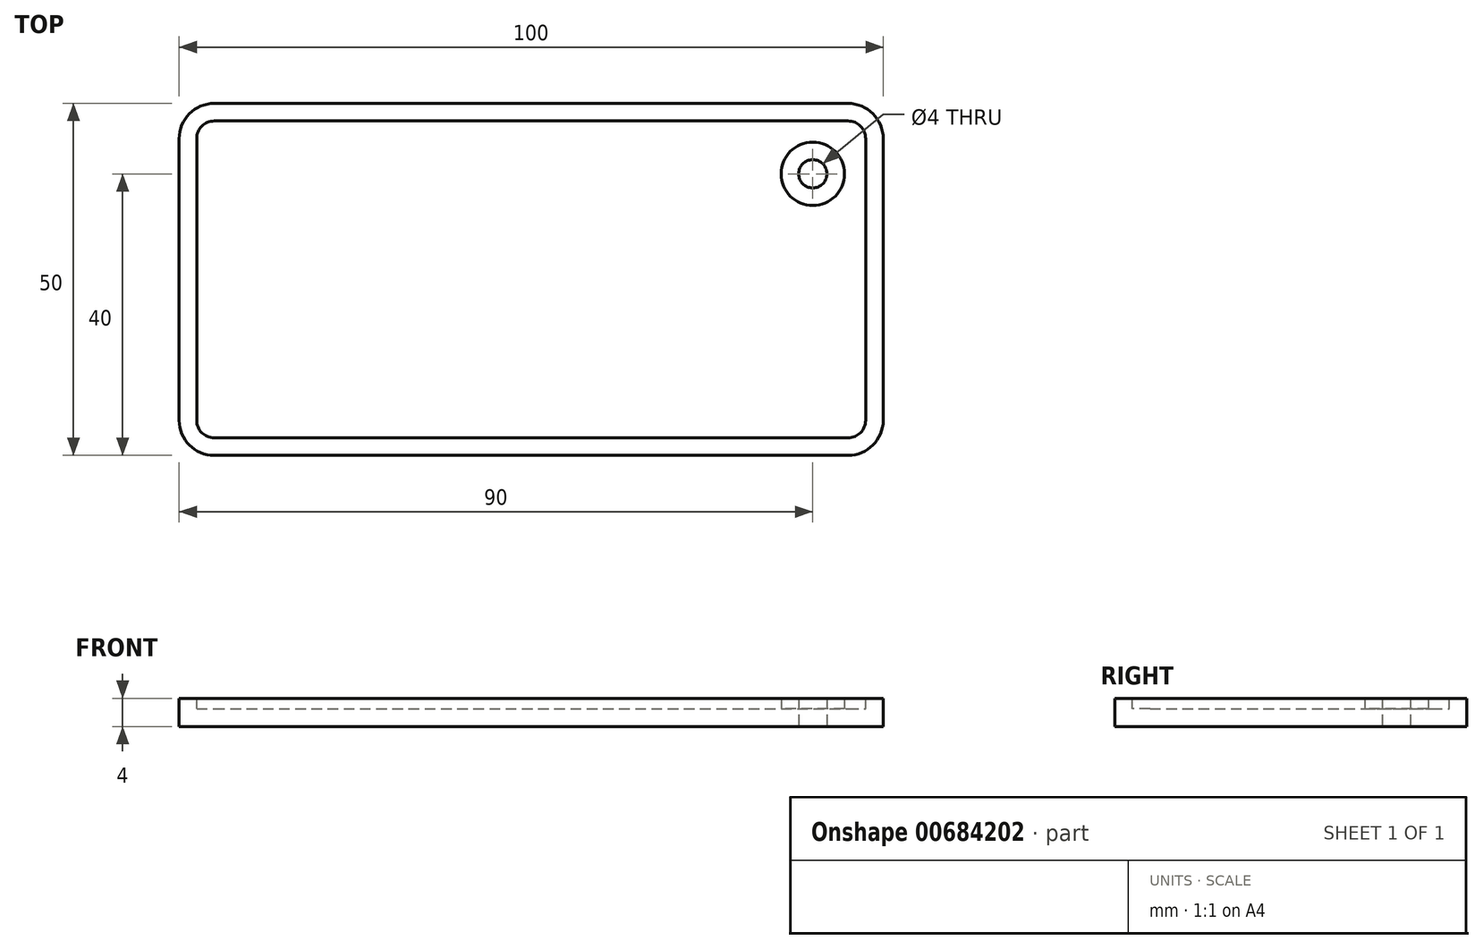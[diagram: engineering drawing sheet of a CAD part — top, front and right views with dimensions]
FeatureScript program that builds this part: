
annotation { "Feature Type Name" : "Feature", "Feature Type Description" : "" }
export const myFeature = defineFeature(function(context is Context, id is Id, definition is map)
    precondition{}
    {
        {
            var Q0;
            Q0=qCreatedBy(makeId("Top.planeOp"),FACE);
            var sketch = newSketch(context, id + "F0", { "sketchPlane" : qUnion([Q0])});
            skLineSegment(sketch, "E0.bottom", {"start": v(5, 0) * mm, "end": v(95, 0) * mm});
            skLineSegment(sketch, "E0.top", {"start": v(5, 50) * mm, "end": v(95, 50) * mm});
            skLineSegment(sketch, "E0.left", {"start": v(0, 5) * mm, "end": v(0, 45) * mm});
            skLineSegment(sketch, "E0.right", {"start": v(100, 5) * mm, "end": v(100, 45) * mm});
            skLineSegment(sketch, "E1.bottom", {"start": v(10, 45) * mm, "end": v(90, 45) * mm});
            skLineSegment(sketch, "E1.top", {"start": v(10, 5) * mm, "end": v(90, 5) * mm});
            skLineSegment(sketch, "E1.left", {"start": v(5, 40) * mm, "end": v(5, 10) * mm});
            skLineSegment(sketch, "E1.right", {"start": v(95, 40) * mm, "end": v(95, 10) * mm});
            skPoint(sketch, "E2.visualSharp", {"position": v(5, 45) * mm});
            skArc(sketch, "E2.filletArc", {"start": v(10, 45) * mm, "mid": v(6.46, 43.54) * mm, "end": v(5, 40) * mm});
            skPoint(sketch, "E3.visualSharp", {"position": v(95, 45) * mm});
            skArc(sketch, "E3.filletArc", {"start": v(95, 40) * mm, "mid": v(93.54, 43.54) * mm, "end": v(90, 45) * mm});
            skPoint(sketch, "E4.visualSharp", {"position": v(95, 5) * mm});
            skArc(sketch, "E4.filletArc", {"start": v(90, 5) * mm, "mid": v(93.54, 6.46) * mm, "end": v(95, 10) * mm});
            skPoint(sketch, "E5.visualSharp", {"position": v(5, 5) * mm});
            skArc(sketch, "E5.filletArc", {"start": v(5, 10) * mm, "mid": v(6.46, 6.46) * mm, "end": v(10, 5) * mm});
            skPoint(sketch, "E6.visualSharp", {"position": v(0, 0) * mm});
            skArc(sketch, "E6.filletArc", {"start": v(0, 5) * mm, "mid": v(1.46, 1.46) * mm, "end": v(5, 0) * mm});
            skPoint(sketch, "E7.visualSharp", {"position": v(100, 0) * mm});
            skArc(sketch, "E7.filletArc", {"start": v(95, 0) * mm, "mid": v(98.54, 1.46) * mm, "end": v(100, 5) * mm});
            skPoint(sketch, "E8.visualSharp", {"position": v(0, 50) * mm});
            skArc(sketch, "E8.filletArc", {"start": v(5, 50) * mm, "mid": v(1.46, 48.54) * mm, "end": v(0, 45) * mm});
            skPoint(sketch, "E9.visualSharp", {"position": v(100, 50) * mm});
            skArc(sketch, "E9.filletArc", {"start": v(100, 45) * mm, "mid": v(98.54, 48.54) * mm, "end": v(95, 50) * mm});
            skSolve(sketch);
        }
        {
            var Q0;
            Q0=makeQuery(id+"F0.imprint","IMPRINT",FACE,{"disambiguationData":[TD([[makeQuery(id+"F0.imprint","IMPRINT",EDGE,{"derivedFrom":sQuery(id+"F0.wireOp",EDGE,"E1.bottom")}),-1.0]])]});
            var Q1;
            Q1=makeQuery(id+"F0.imprint","IMPRINT",FACE,{"disambiguationData":[TD([[makeQuery(id+"F0.imprint","IMPRINT",EDGE,{"derivedFrom":sQuery(id+"F0.wireOp",EDGE,"E0.bottom")}),1.0]])]});
            extrude(context, id + "F1", {"entities" : qUnion([Q0, Q1]), "depth" : 4 * mm, "offsetDistance" : 25 * mm});
        }
        {
            var Q0;
            Q0=sQuery(id+"F0.wireOp",VERTEX,"E3.filletArc.center");
            var Q1;
            Q1=makeQuery(id+"F1.opExtrude","SWEPT_BODY",BODY,{"disambiguationData":[OSD([sQuery(id+"F0.wireOp",EDGE,"E0.bottom"),sQuery(id+"F0.wireOp",EDGE,"E0.top"),sQuery(id+"F0.wireOp",EDGE,"E0.left"),sQuery(id+"F0.wireOp",EDGE,"E0.right"),sQuery(id+"F0.wireOp",EDGE,"E6.filletArc"),sQuery(id+"F0.wireOp",EDGE,"E7.filletArc"),sQuery(id+"F0.wireOp",EDGE,"E8.filletArc"),sQuery(id+"F0.wireOp",EDGE,"E9.filletArc")])]});
            hole(context, id + "F2", {"style" : HoleStyle.SIMPLE, "endStyle" : HoleEndStyle.THROUGH, "oppositeDirection" : true, "holeDiameter" : 4 * mm, "majorDiameter" : 5 * mm, "isTappedThrough" : true, "tappedDepth" : 12 * mm, "tapClearance" : 3, "locations" : qUnion([Q0]), "scope" : qUnion([Q1])});
        }
        {
            var Q0;
            Q0=makeQuery(id+"F1.opExtrude","CAP_FACE",FACE,{"disambiguationData":[OSD([sQuery(id+"F0.wireOp",EDGE,"E0.bottom"),sQuery(id+"F0.wireOp",EDGE,"E0.top"),sQuery(id+"F0.wireOp",EDGE,"E0.left"),sQuery(id+"F0.wireOp",EDGE,"E0.right"),sQuery(id+"F0.wireOp",EDGE,"E6.filletArc"),sQuery(id+"F0.wireOp",EDGE,"E7.filletArc"),sQuery(id+"F0.wireOp",EDGE,"E8.filletArc"),sQuery(id+"F0.wireOp",EDGE,"E9.filletArc")])],"isStart":false});
            var Q1;
            Q1=makeQuery(id+"F1.opExtrude","SWEPT_BODY",BODY,{"disambiguationData":[OSD([sQuery(id+"F0.wireOp",EDGE,"E0.bottom"),sQuery(id+"F0.wireOp",EDGE,"E0.top"),sQuery(id+"F0.wireOp",EDGE,"E0.left"),sQuery(id+"F0.wireOp",EDGE,"E0.right"),sQuery(id+"F0.wireOp",EDGE,"E6.filletArc"),sQuery(id+"F0.wireOp",EDGE,"E7.filletArc"),sQuery(id+"F0.wireOp",EDGE,"E8.filletArc"),sQuery(id+"F0.wireOp",EDGE,"E9.filletArc")])]});
            shell(context, id + "F3", {"entities" : qUnion([Q0]), "parts" : qUnion([Q1]), "thickness" : 2.5 * mm});
        }
    });
